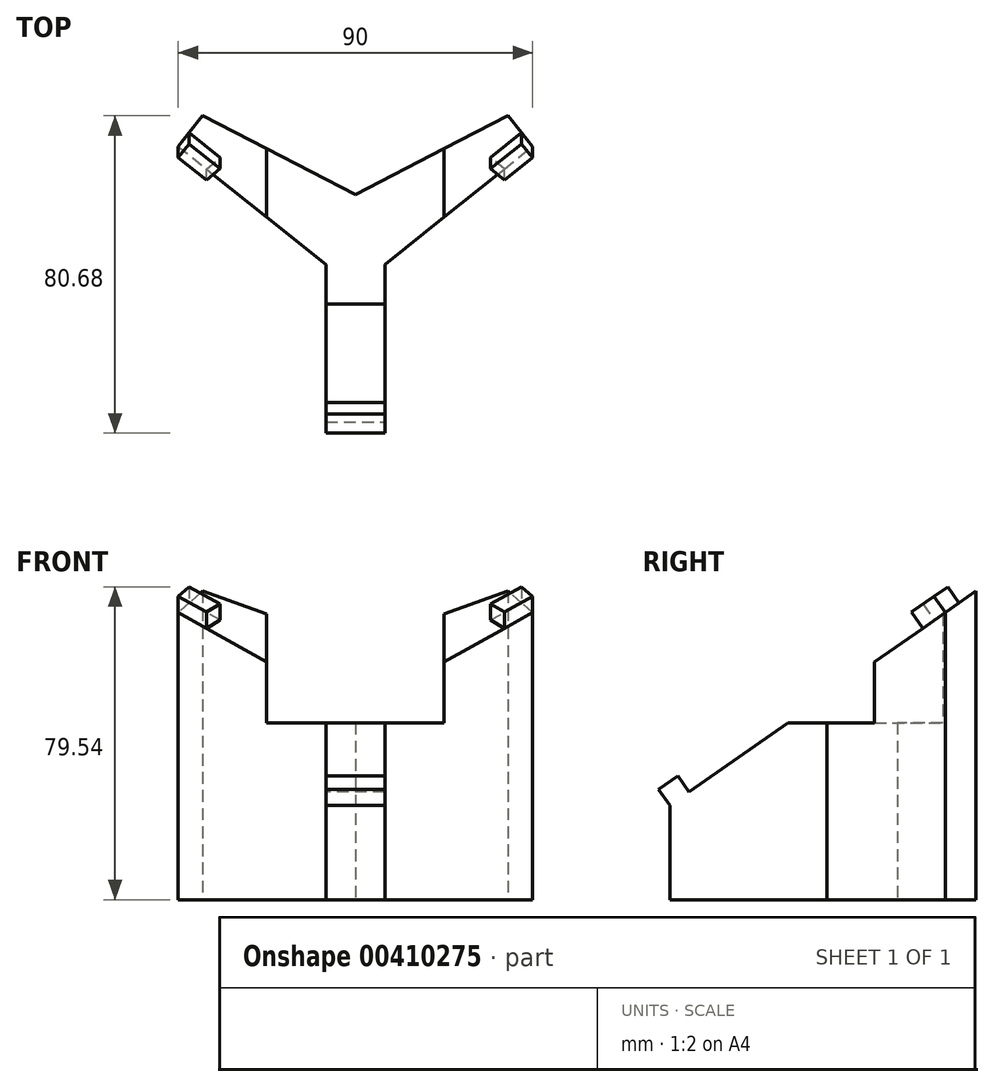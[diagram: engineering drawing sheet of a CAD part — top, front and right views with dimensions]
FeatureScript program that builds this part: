
annotation { "Feature Type Name" : "Feature", "Feature Type Description" : "" }
export const myFeature = defineFeature(function(context is Context, id is Id, definition is map)
    precondition{}
    {
        {
            var Q0;
            Q0=qCreatedBy(makeId("Top.planeOp"),FACE);
            var sketch = newSketch(context, id + "F0", { "sketchPlane" : qUnion([Q0])});
            skLineSegment(sketch, "E0", {"start": v(-45, 25) * mm, "end": v(-7.5, -5) * mm});
            skLineSegment(sketch, "E1", {"start": v(-7.5, -5) * mm, "end": v(-7.5, -45) * mm});
            skLineSegment(sketch, "E2", {"start": v(-7.5, -45) * mm, "end": v(7.5, -45) * mm});
            skLineSegment(sketch, "E3", {"start": v(7.5, -45) * mm, "end": v(7.5, -5) * mm});
            skLineSegment(sketch, "E4", {"start": v(7.5, -5) * mm, "end": v(45, 25) * mm});
            skLineSegment(sketch, "E5", {"start": v(45, 25) * mm, "end": v(38.75, 32.8) * mm});
            skLineSegment(sketch, "E6", {"start": v(38.75, 32.8) * mm, "end": v(0, 12.8) * mm});
            skLineSegment(sketch, "E7", {"start": v(0, 12.8) * mm, "end": v(-38.75, 32.8) * mm});
            skLineSegment(sketch, "E8", {"start": v(-38.75, 32.8) * mm, "end": v(-45, 25) * mm});
            skSolve(sketch);
        }
        {
            var Q0;
            Q0 = qSketchRegion(id + "F0", true);
            extrude(context, id + "F1", {"entities" : qUnion([Q0]), "depth" : 80 * mm});
        }
        {
            var Q0;
            Q0=makeQuery(id+"F1.opExtrude","SWEPT_FACE",FACE,{"disambiguationData":[OSD([sQuery(id+"F0.wireOp",EDGE,"E1")])]});
            var sketch = newSketch(context, id + "F2", { "sketchPlane" : qUnion([Q0])});
            skLineSegment(sketch, "E9", {"start": v(45, 80) * mm, "end": v(-35, 80) * mm});
            skPoint(sketch, "E9.endSnap0", {"position": v(25, 80) * mm});
            skLineSegment(sketch, "E10", {"start": v(-35, 80) * mm, "end": v(45, 23.98) * mm});
            skLineSegment(sketch, "E11", {"start": v(45, 23.98) * mm, "end": v(45, 80) * mm});
            skSolve(sketch);
        }
        {
            var Q0;
            Q0 = qSketchRegion(id + "F2", true);
            extrude(context, id + "F3", {"entities" : qUnion([Q0]), "operationType" : NewBodyOperationType.REMOVE, "endBound" : BoundingType.THROUGH_ALL, "depth" : 25 * mm, "hasSecondDirection" : true, "secondDirectionBound" : SecondDirectionBoundingType.THROUGH_ALL, "secondDirectionOppositeDirection" : true, "secondDirectionDepth" : 25 * mm});
        }
        {
            var Q0;
            Q0=makeQuery(id+"F3.boolean.opBoolean","COPY",FACE,{"derivedFrom":makeQuery(id+"F3.opExtrude","SWEPT_FACE",FACE,{"disambiguationData":[OSD([sQuery(id+"F2.wireOp",EDGE,"E10")])]})});
            var sketch = newSketch(context, id + "F4", { "sketchPlane" : qUnion([Q0])});
            skLineSegment(sketch, "E12", {"start": v(-45, 62.35) * mm, "end": v(-37.85, 55.36) * mm});
            skLineSegment(sketch, "E13", {"start": v(-37.85, 55.36) * mm, "end": v(-34.35, 58.94) * mm});
            skLineSegment(sketch, "E14", {"start": v(-34.35, 58.94) * mm, "end": v(-42.2, 66.61) * mm});
            skLineSegment(sketch, "E15", {"start": v(-42.2, 66.61) * mm, "end": v(-45, 62.35) * mm});
            skLineSegment(sketch, "E16", {"start": v(45, 62.35) * mm, "end": v(37.85, 55.36) * mm});
            skLineSegment(sketch, "E17", {"start": v(37.85, 55.36) * mm, "end": v(34.35, 58.94) * mm});
            skLineSegment(sketch, "E18", {"start": v(34.35, 58.94) * mm, "end": v(42.2, 66.61) * mm});
            skLineSegment(sketch, "E19", {"start": v(42.2, 66.61) * mm, "end": v(45, 62.35) * mm});
            skLineSegment(sketch, "E20", {"start": v(-7.5, -23.1) * mm, "end": v(7.5, -23.1) * mm});
            skLineSegment(sketch, "E21", {"start": v(7.5, -23.1) * mm, "end": v(7.5, -17.1) * mm});
            skLineSegment(sketch, "E22", {"start": v(7.5, -17.1) * mm, "end": v(-7.5, -17.1) * mm});
            skLineSegment(sketch, "E23", {"start": v(-7.5, -17.1) * mm, "end": v(-7.5, -23.1) * mm});
            skSolve(sketch);
        }
        {
            var Q0;
            Q0 = qSketchRegion(id + "F4", true);
            extrude(context, id + "F5", {"entities" : qUnion([Q0]), "operationType" : NewBodyOperationType.ADD, "depth" : 5 * mm});
        }
        {
            var Q0;
            Q0=makeQuery(id+"F5.boolean.opBoolean","MERGE",FACE,{"derivedFrom":[makeQuery(id+"F1.opExtrude","SWEPT_FACE",FACE,{"disambiguationData":[OSD([sQuery(id+"F0.wireOp",EDGE,"E1")])]}),makeQuery(id+"F5.opExtrude","SWEPT_FACE",FACE,{"disambiguationData":[OSD([sQuery(id+"F4.wireOp",EDGE,"E23")])]})]});
            var sketch = newSketch(context, id + "F6", { "sketchPlane" : qUnion([Q0])});
            skLineSegment(sketch, "E24", {"start": v(14.99, 45) * mm, "end": v(-25.01, 45) * mm});
            skLineSegment(sketch, "E25", {"start": v(-25.01, 45) * mm, "end": v(-25.01, 73) * mm});
            skLineSegment(sketch, "E26", {"start": v(-25.01, 73) * mm, "end": v(14.99, 45) * mm});
            skSolve(sketch);
        }
        {
            var Q0;
            Q0 = qSketchRegion(id + "F6", true);
            extrude(context, id + "F7", {"entities" : qUnion([Q0]), "operationType" : NewBodyOperationType.REMOVE, "oppositeDirection" : true, "depth" : 30 * mm, "hasSecondDirection" : true, "secondDirectionOppositeDirection" : false, "secondDirectionDepth" : 15 * mm});
        }
    });
